# Revit family: QF_ELECTROLUXPROFESSIONAL_1LSNLE_IC64825R_S
name_source: partatom
category: Attrezzature speciali
units: mm (PartAtom-declared; Revit-internal decimal feet)

## family parameters
Basato su piano di lavoro = No
Condiviso = No
Punto di calcolo locali = No
Quota connettore circolare = Usa diametro
Sempre verticale = Sì
Taglio con vuoti quando caricato = No
Tipo di parte = Normale

## types (1)
- QF_ELECTROLUXPROFESSIONAL_1LSNLE_IC64825R_S
    -B/2 = -1270 mm  [stored -4.16667 ft]
    A_Width = 3205 mm
    B_2 = 1270 mm  [stored 4.16667 ft]
    B_IronerWidth = 2540 mm
    C_WithBetweenFeet = 2930 mm  [stored 9.61286 ft]
    DepthMax = 1100 mm
    DepthPedestal = 950 mm  [stored 3.1168 ft]
    Feet = 80 mm  [stored 0.262467 ft]
    Height = 1270 mm  [stored 4.16667 ft]
    Prospetto di default = 0 mm  [stored 0 ft]

note: [stored X ft] marks values corroborated as IEEE doubles in the binary element streams (Revit-internal decimal feet)

## geometry (parser evidence)
native form markers: Sweep x11
no freeform markers — native parametric forms only
